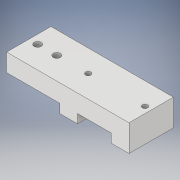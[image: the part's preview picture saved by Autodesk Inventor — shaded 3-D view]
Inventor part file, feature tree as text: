
AUTODESK INVENTOR PART (.ipt)
format: ipt  version: 2019 (Build 230136000, 136)  size: 135,168 bytes
history: native  units: mm
features: extrude x2, sketch x2
ambient origin geometry x8: Origin, YZ Plane, XZ Plane, XY Plane, X Axis, Y Axis, Z Axis, Center Point
bodies: Solid1 (feature_tree)
feature tree (4):
  extrude  "Extrusion1"  Depth=10.0mm
  extrude  "Extrusion2"  Depth=30.0mm
  sketch  "Sketch1"  dims[d0=19.0mm d1=10.0mm]
  sketch  "Sketch2"  dims[d2=10.0mm d3=30.0mm d4=10.0mm d5=5.0mm d6=59.0mm d7=10.0mm d8=25.0mm d9=0.0mm d10=4.0mm d11=4.0mm d15=12.5mm d16=12.5mm d17=15.0mm d18=0.0mm d19=5.0mm d20=10.8mm d22=3.0mm d24=3.5mm d26=12.5mm d28=12.5mm d29=3.0mm d30=3.5mm]
